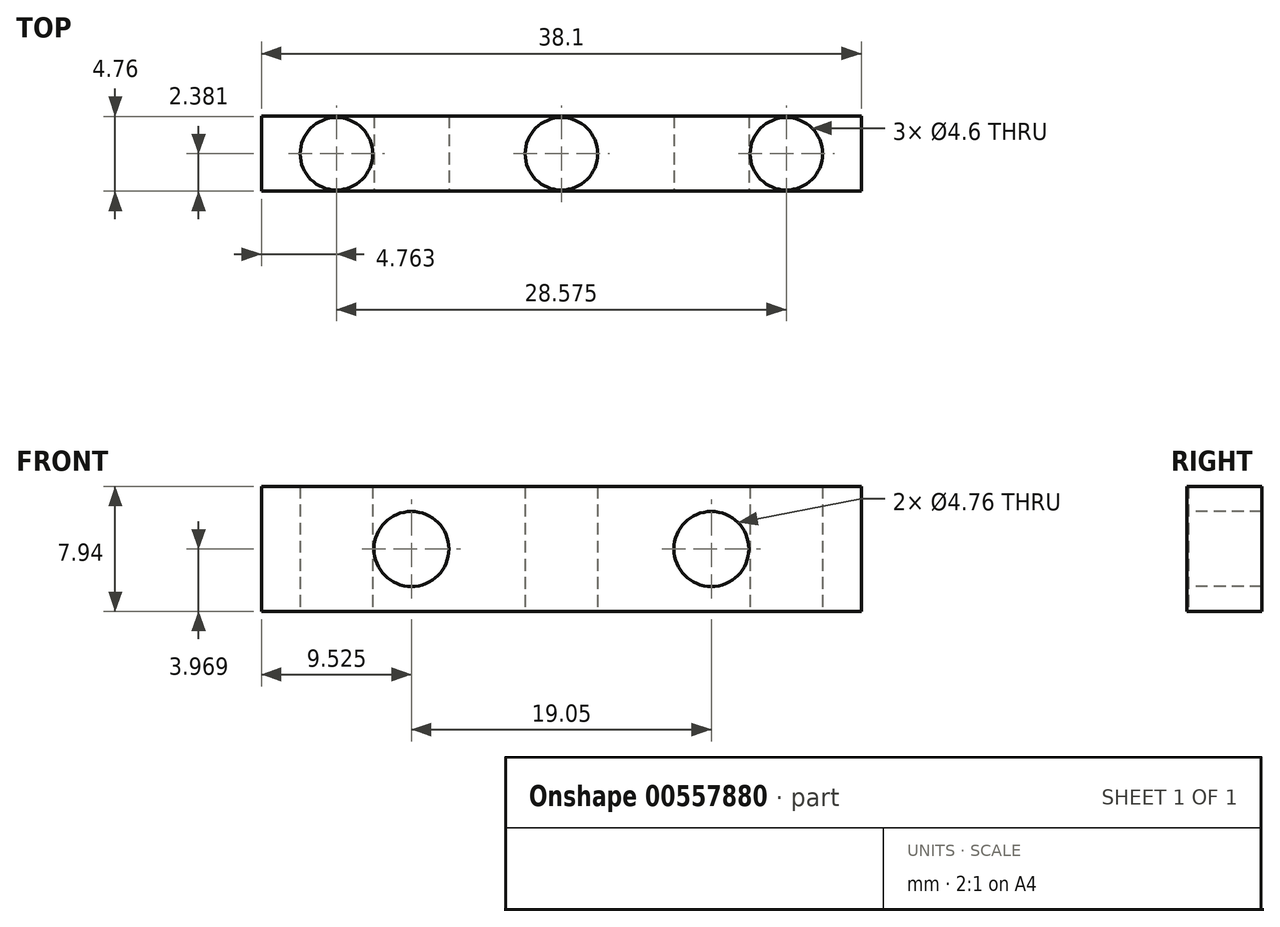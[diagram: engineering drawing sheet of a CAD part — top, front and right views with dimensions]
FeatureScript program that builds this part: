
annotation { "Feature Type Name" : "Feature", "Feature Type Description" : "" }
export const myFeature = defineFeature(function(context is Context, id is Id, definition is map)
    precondition{}
    {
        {
            var Q0;
            Q0=qCreatedBy(makeId("Top.planeOp"),FACE);
            var sketch = newSketch(context, id + "F0", { "sketchPlane" : qUnion([Q0])});
            skLineSegment(sketch, "E0.bottom", {"start": v(0, 0) * mm, "end": v(38.1, 0) * mm});
            skLineSegment(sketch, "E0.top", {"start": v(0, 4.76) * mm, "end": v(38.1, 4.76) * mm});
            skLineSegment(sketch, "E0.left", {"start": v(0, 0) * mm, "end": v(0, 4.76) * mm});
            skLineSegment(sketch, "E0.right", {"start": v(38.1, 0) * mm, "end": v(38.1, 4.76) * mm});
            skCircle(sketch, "E1", {"center": v(19.05, 2.38) * mm, "radius": 2.3 * mm});
            skCircle(sketch, "E2", {"center": v(33.34, 2.38) * mm, "radius": 2.3 * mm});
            skCircle(sketch, "E3", {"center": v(4.76, 2.38) * mm, "radius": 2.3 * mm});
            skSolve(sketch);
        }
        {
            var Q0;
            {var subQ0=sQuery(id+"F0.wireOp",EDGE,"E0.left");Q0=makeQuery(id+"F0.imprint","IMPRINT",FACE,{"disambiguationData":[TD([[makeQuery(id+"F0.imprint","IMPRINT",EDGE,{"derivedFrom":subQ0}),-1.0]])]});}
            var Q1;
            {var subQ0=sQuery(id+"F0.wireOp",EDGE,"E0.right");Q1=makeQuery(id+"F0.imprint","IMPRINT",FACE,{"disambiguationData":[TD([[makeQuery(id+"F0.imprint","IMPRINT",EDGE,{"derivedFrom":subQ0}),1.0]])]});}
            extrude(context, id + "F1", {"entities" : qUnion([Q0, Q1]), "depth" : 7.94 * mm, "offsetDistance" : 25.4 * mm});
        }
        {
            var Q0;
            Q0=makeQuery(id+"F1.opExtrude","SWEPT_FACE",FACE,{"disambiguationData":[OSD([sQuery(id+"F0.wireOp",EDGE,"E0.bottom")])]});
            var sketch = newSketch(context, id + "F2", { "sketchPlane" : qUnion([Q0])});
            skCircle(sketch, "E4", {"center": v(28.58, 3.97) * mm, "radius": 2.38 * mm});
            skCircle(sketch, "E5", {"center": v(9.53, 3.97) * mm, "radius": 2.38 * mm});
            skSolve(sketch);
        }
        {
            var Q0;
            Q0=makeQuery(id+"F2.imprint","IMPRINT",FACE,{"disambiguationData":[TD([[makeQuery(id+"F2.imprint","IMPRINT",EDGE,{"derivedFrom":sQuery(id+"F2.wireOp",EDGE,"E4")}),1.0]])]});
            var Q1;
            Q1=makeQuery(id+"F2.imprint","IMPRINT",FACE,{"disambiguationData":[TD([[makeQuery(id+"F2.imprint","IMPRINT",EDGE,{"derivedFrom":sQuery(id+"F2.wireOp",EDGE,"E5")}),1.0]])]});
            extrude(context, id + "F3", {"entities" : qUnion([Q0, Q1]), "operationType" : NewBodyOperationType.REMOVE, "oppositeDirection" : true, "depth" : 25.4 * mm, "offsetDistance" : 25.4 * mm});
        }
    });
